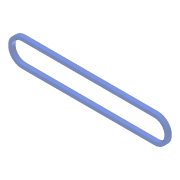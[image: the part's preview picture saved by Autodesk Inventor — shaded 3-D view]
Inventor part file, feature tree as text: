
AUTODESK INVENTOR PART (.ipt)
format: ipt  version: 2015 (Build 190159000, 159)  size: 89,088 bytes
history: native  units: in
note: dims shown in document units (in); Inventor stores cm internally (conversion verified against a paired STEP export)
features: extrude x1, other x1, sketch x1
ambient origin geometry x8: Origin, YZ Plane, XZ Plane, XY Plane, X Axis, Y Axis, Z Axis, Center Point
bodies: Solid1 (feature_tree)
feature tree (3):
  extrude  "Extrusion1"  Depth=0.3in
  other  "Work Axis1"
  sketch  "Sketch1"  dims[d1=0.8754in d2=0.8754in d3=0.125in d4=0.125in d8=0.3in d9=0.0in]
